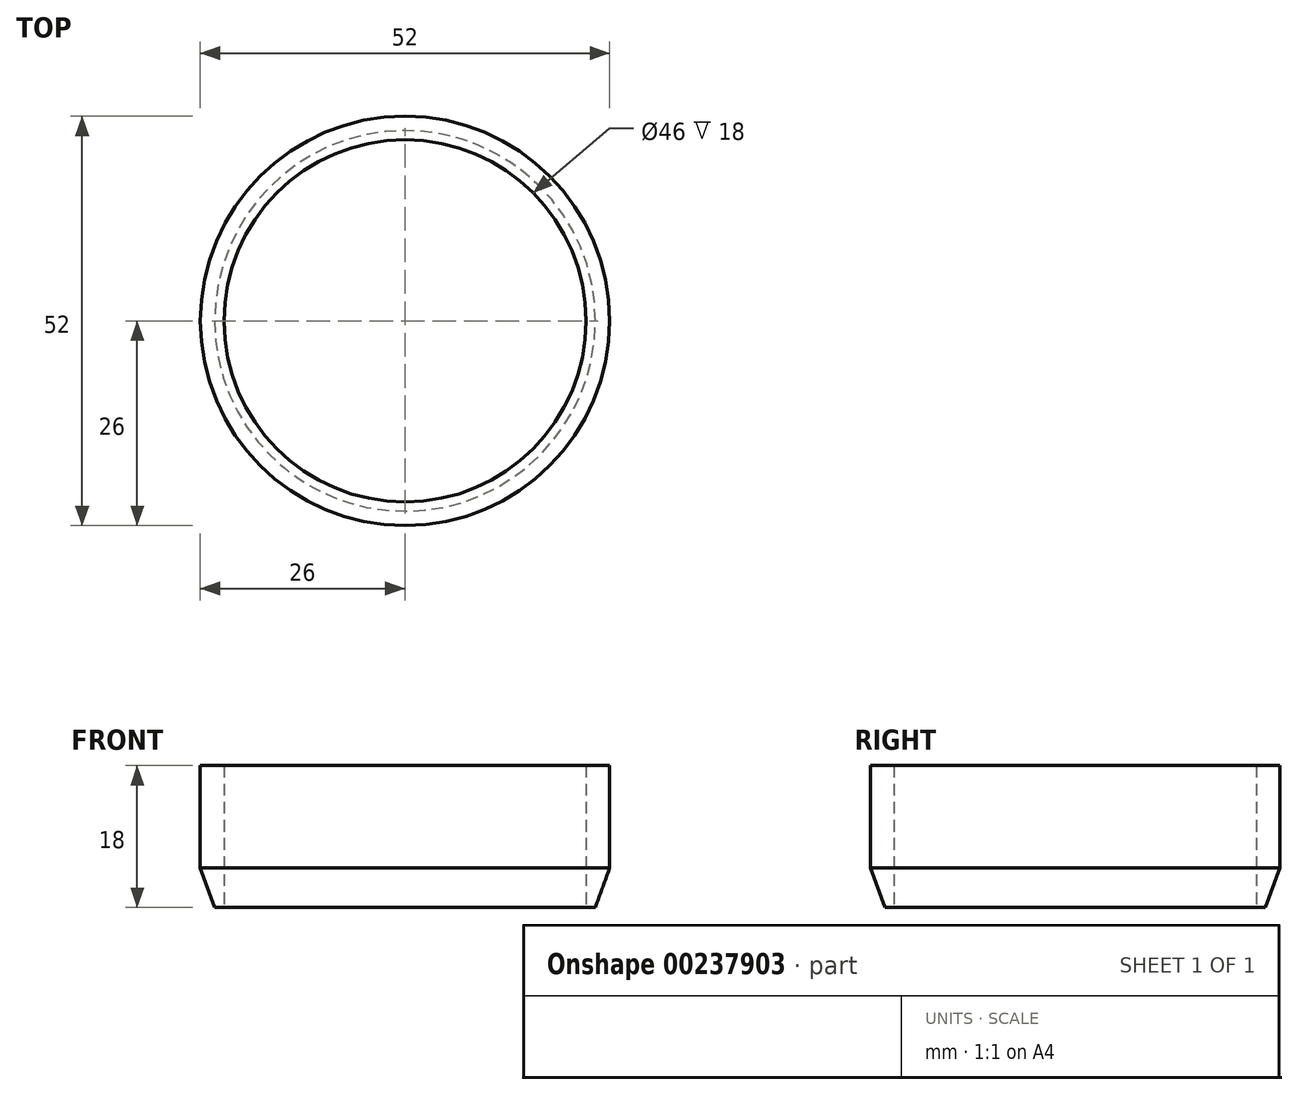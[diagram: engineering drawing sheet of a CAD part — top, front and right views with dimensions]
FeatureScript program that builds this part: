
annotation { "Feature Type Name" : "Feature", "Feature Type Description" : "" }
export const myFeature = defineFeature(function(context is Context, id is Id, definition is map)
    precondition{}
    {
        {
            var Q0;
            Q0=qCreatedBy(makeId("Top.planeOp"),FACE);
            var sketch = newSketch(context, id + "F0", { "sketchPlane" : qUnion([Q0])});
            skCircle(sketch, "E0", {"center": v(0, 0) * mm, "radius": 23 * mm});
            skCircle(sketch, "E1", {"center": v(0, 0) * mm, "radius": 26 * mm});
            skCircle(sketch, "E2", {"center": v(0, 0) * mm, "radius": 10 * mm});
            skCircle(sketch, "E3", {"center": v(0, 0) * mm, "radius": 7 * mm});
            skLineSegment(sketch, "E4", {"start": v(-3, 9.54) * mm, "end": v(-3, 22.8) * mm});
            skLineSegment(sketch, "E5", {"start": v(3, 9.54) * mm, "end": v(3, 22.8) * mm});
            skLineSegment(sketch, "E6.1.0", {"start": v(-9.76, -2.17) * mm, "end": v(-21.25, -8.8) * mm});
            skLineSegment(sketch, "E6.1.1", {"start": v(-6.76, -7.37) * mm, "end": v(-18.25, -14) * mm});
            skLineSegment(sketch, "E6.2.0", {"start": v(6.76, -7.37) * mm, "end": v(18.25, -14) * mm});
            skLineSegment(sketch, "E6.2.1", {"start": v(9.76, -2.17) * mm, "end": v(21.25, -8.8) * mm});
            skSolve(sketch);
        }
        {
            var Q0;
            Q0=makeQuery(id+"F0.imprint","IMPRINT",FACE,{"disambiguationData":[TD([[makeQuery(id+"F0.imprint","IMPRINT",EDGE,{"derivedFrom":sQuery(id+"F0.wireOp",EDGE,"E1")}),1.0]])]});
            extrude(context, id + "F1", {"entities" : qUnion([Q0]), "depth" : 3 * mm, "offsetDistance" : 25 * mm});
        }
        {
            var Q0;
            Q0=makeQuery(id+"F0.imprint","IMPRINT",FACE,{"disambiguationData":[TD([[makeQuery(id+"F0.imprint","IMPRINT",EDGE,{"derivedFrom":sQuery(id+"F0.wireOp",EDGE,"E1")}),1.0]])]});
            extrude(context, id + "F2", {"entities" : qUnion([Q0]), "operationType" : NewBodyOperationType.ADD, "oppositeDirection" : true, "depth" : 15 * mm, "offsetDistance" : 25 * mm});
        }
        {
            var Q0;
            Q0=makeQuery(id+"F2.opExtrude","CAP_EDGE",EDGE,{"disambiguationData":[OSD([sQuery(id+"F0.wireOp",EDGE,"E1")])],"isStart":false});
            chamfer(context, id + "F3", {"entities" : qUnion([Q0]), "chamferType" : ChamferType.OFFSET_ANGLE, "width" : 5 * mm, "oppositeDirection" : false, "angle" : 20 * degree, "tangentPropagation" : true});
        }
    });
